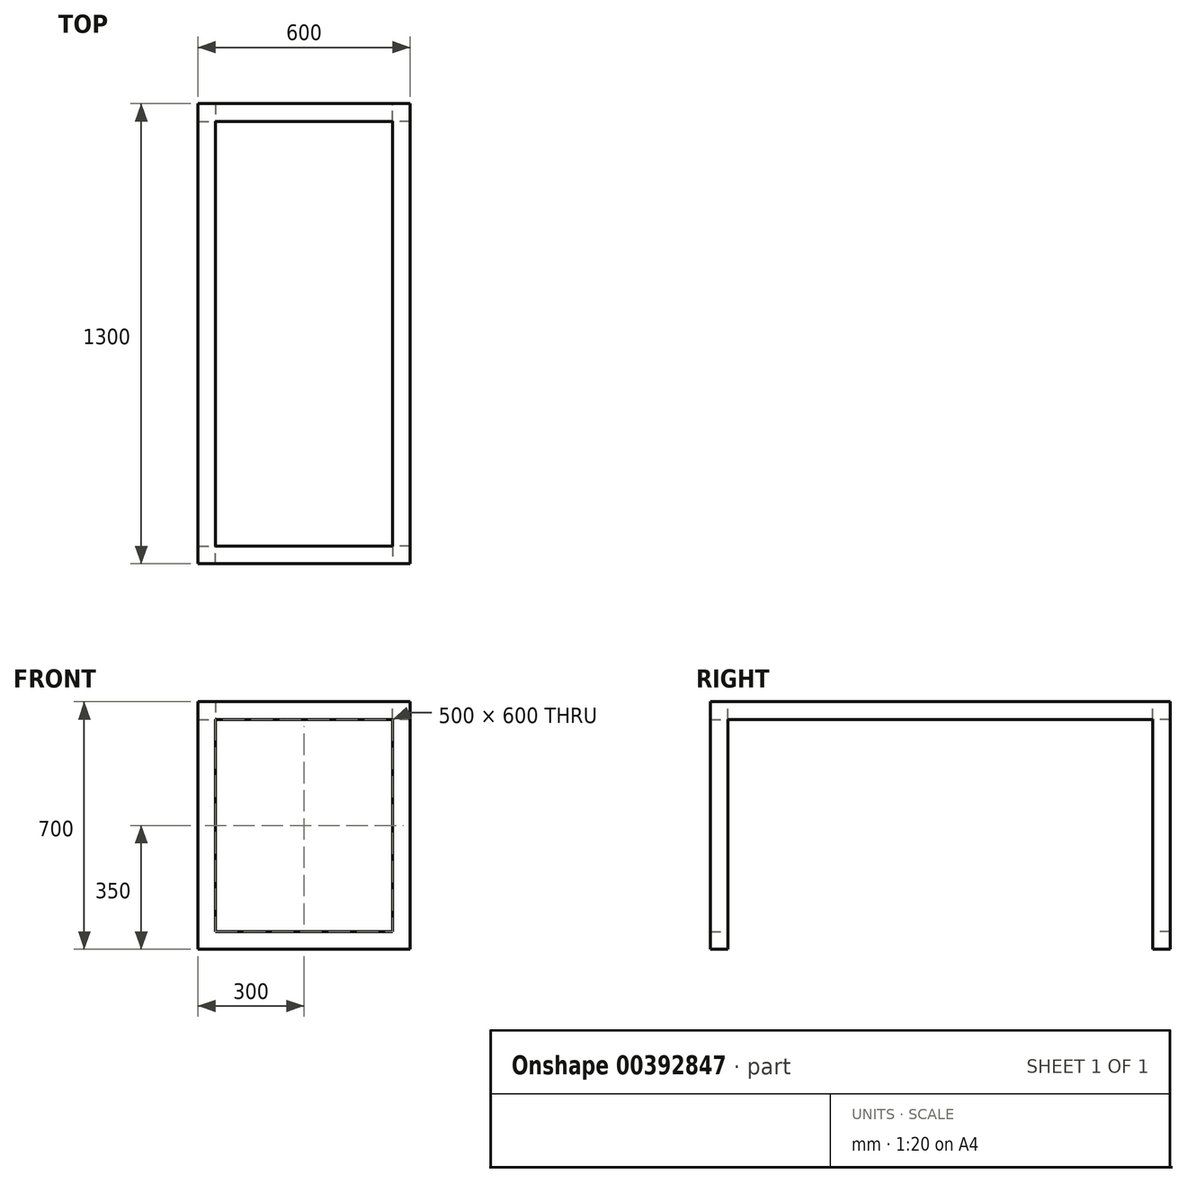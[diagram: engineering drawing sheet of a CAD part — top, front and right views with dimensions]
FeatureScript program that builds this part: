
annotation { "Feature Type Name" : "Feature", "Feature Type Description" : "" }
export const myFeature = defineFeature(function(context is Context, id is Id, definition is map)
    precondition{}
    {
        {
            var Q0;
            Q0=qCreatedBy(makeId("Front.planeOp"),FACE);
            var sketch = newSketch(context, id + "F0", { "sketchPlane" : qUnion([Q0])});
            skLineSegment(sketch, "E0.bottom", {"start": v(-300, 0) * mm, "end": v(300, 0) * mm});
            skLineSegment(sketch, "E0.top", {"start": v(-300, 700) * mm, "end": v(300, 700) * mm});
            skLineSegment(sketch, "E0.left", {"start": v(-300, 0) * mm, "end": v(-300, 700) * mm});
            skLineSegment(sketch, "E0.right", {"start": v(300, 0) * mm, "end": v(300, 700) * mm});
            skLineSegment(sketch, "E1.bottom", {"start": v(-250, 50) * mm, "end": v(250, 50) * mm});
            skLineSegment(sketch, "E1.left", {"start": v(-250, 50) * mm, "end": v(-250, 700) * mm});
            skLineSegment(sketch, "E1.right", {"start": v(250, 50) * mm, "end": v(250, 700) * mm});
            skSolve(sketch);
        }
        {
            var Q0;
            Q0=makeQuery(id+"F0.imprint","IMPRINT",FACE,{"disambiguationData":[TD([[makeQuery(id+"F0.imprint","IMPRINT",EDGE,{"derivedFrom":sQuery(id+"F0.wireOp",EDGE,"E0.bottom")}),1.0]])]});
            extrude(context, id + "F1", {"entities" : qUnion([Q0]), "depth" : 50 * mm});
        }
        {
            var Q0;
            Q0=makeQuery(id+"F1.opExtrude","CAP_FACE",FACE,{"disambiguationData":[OSD([sQuery(id+"F0.wireOp",EDGE,"E0.bottom"),sQuery(id+"F0.wireOp",EDGE,"E0.top"),sQuery(id+"F0.wireOp",EDGE,"E0.left"),sQuery(id+"F0.wireOp",EDGE,"E0.right"),sQuery(id+"F0.wireOp",EDGE,"E1.bottom"),sQuery(id+"F0.wireOp",EDGE,"E1.left"),sQuery(id+"F0.wireOp",EDGE,"E1.right")])],"isStart":true});
            var sketch = newSketch(context, id + "F2", { "sketchPlane" : qUnion([Q0])});
            skLineSegment(sketch, "E2.bottom", {"start": v(-300, 700) * mm, "end": v(-250, 700) * mm});
            skLineSegment(sketch, "E2.top", {"start": v(-300, 650) * mm, "end": v(-250, 650) * mm});
            skLineSegment(sketch, "E2.left", {"start": v(-300, 700) * mm, "end": v(-300, 650) * mm});
            skLineSegment(sketch, "E2.right", {"start": v(-250, 700) * mm, "end": v(-250, 650) * mm});
            skSolve(sketch);
        }
        {
            var Q0;
            Q0=makeQuery(id+"F2.imprint","IMPRINT",FACE,{"disambiguationData":[TD([[makeQuery(id+"F2.imprint","IMPRINT",EDGE,{"derivedFrom":sQuery(id+"F2.wireOp",EDGE,"E2.bottom")}),1.0]])]});
            extrude(context, id + "F3", {"entities" : qUnion([Q0]), "depth" : 600 * mm});
        }
        {
            var Q0;
            Q0=makeQuery(id+"F3.opExtrude","SWEPT_BODY",BODY,{"disambiguationData":[OSD([sQuery(id+"F2.wireOp",EDGE,"E2.bottom"),sQuery(id+"F2.wireOp",EDGE,"E2.top"),sQuery(id+"F2.wireOp",EDGE,"E2.left"),sQuery(id+"F2.wireOp",EDGE,"E2.right")])]});
            var Q1;
            Q1=qCreatedBy(makeId("Right.planeOp"),FACE);
            mirror(context, id + "F4", {"operationType" : NewBodyOperationType.ADD, "entities" : qUnion([Q0]), "mirrorPlane" : qUnion([Q1])});
        }
        {
            var Q0;
            {var subQ0=makeQuery(id+"F4.boolean.opBoolean","MERGE",FACE,{"derivedFrom":[makeQuery(id+"F1.opExtrude","SWEPT_FACE",FACE,{"disambiguationData":[OSD([sQuery(id+"F0.wireOp",EDGE,"E1.left")])]}),makeQuery(id+"F4.opPattern","COPY",FACE,{"derivedFrom":makeQuery(id+"F3.opExtrude","SWEPT_FACE",FACE,{"disambiguationData":[OSD([sQuery(id+"F2.wireOp",EDGE,"E2.right")])]}),"instanceName":"1"})]});Q0=makeQuery(id+"F7.boolean.opBoolean","MERGE",FACE,{"derivedFrom":[subQ0,makeQuery(id+"F7.opPattern","COPY",FACE,{"derivedFrom":subQ0,"instanceName":"1"})]});}
            var sketch = newSketch(context, id + "F5", { "sketchPlane" : qUnion([Q0])});
            skLineSegment(sketch, "E3.bottom", {"start": v(-50, 700) * mm, "end": v(0, 700) * mm});
            skLineSegment(sketch, "E3.top", {"start": v(-50, 650) * mm, "end": v(0, 650) * mm});
            skLineSegment(sketch, "E3.left", {"start": v(-50, 700) * mm, "end": v(-50, 650) * mm});
            skLineSegment(sketch, "E3.right", {"start": v(0, 700) * mm, "end": v(0, 650) * mm});
            skSolve(sketch);
        }
        {
            var Q0;
            Q0=makeQuery(id+"F5.imprint","IMPRINT",FACE,{"disambiguationData":[TD([[makeQuery(id+"F5.imprint","IMPRINT",EDGE,{"derivedFrom":sQuery(id+"F5.wireOp",EDGE,"E3.bottom")}),-1.0]])]});
            extrude(context, id + "F6", {"entities" : qUnion([Q0]), "operationType" : NewBodyOperationType.ADD, "endBound" : BoundingType.UP_TO_NEXT, "depth" : 25 * mm, "hasSecondDirection" : true, "secondDirectionOppositeDirection" : true, "secondDirectionDepth" : 25 * mm});
        }
        {
            var Q0;
            Q0=makeQuery(id+"F1.opExtrude","SWEPT_BODY",BODY,{"disambiguationData":[OSD([sQuery(id+"F0.wireOp",EDGE,"E0.bottom"),sQuery(id+"F0.wireOp",EDGE,"E0.top"),sQuery(id+"F0.wireOp",EDGE,"E0.left"),sQuery(id+"F0.wireOp",EDGE,"E0.right"),sQuery(id+"F0.wireOp",EDGE,"E1.bottom"),sQuery(id+"F0.wireOp",EDGE,"E1.left"),sQuery(id+"F0.wireOp",EDGE,"E1.right")])]});
            var Q1;
            Q1=makeQuery(id+"F3.opExtrude","CAP_FACE",FACE,{"disambiguationData":[OSD([sQuery(id+"F2.wireOp",EDGE,"E2.bottom"),sQuery(id+"F2.wireOp",EDGE,"E2.top"),sQuery(id+"F2.wireOp",EDGE,"E2.left"),sQuery(id+"F2.wireOp",EDGE,"E2.right")])],"isStart":false});
            mirror(context, id + "F7", {"operationType" : NewBodyOperationType.ADD, "entities" : qUnion([Q0]), "mirrorPlane" : qUnion([Q1])});
        }
    });
